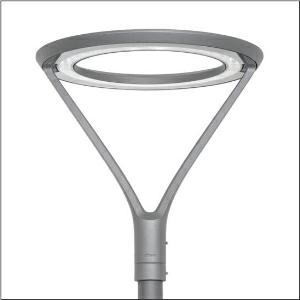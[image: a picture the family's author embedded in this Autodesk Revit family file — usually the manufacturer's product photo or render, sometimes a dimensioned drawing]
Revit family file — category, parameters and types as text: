
# Revit family: dl_r__20___pl1_2s_5xa512832s008_323f
name_source: partatom
category: Lighting Fixtures
units: mm (PartAtom-declared; Revit-internal decimal feet)

## family parameters
Cut with Voids When Loaded = No
Host = Face
Light Source = No
Part Type = Normal
Room Calculation Point = No
Round Connector Dimension = Use Diameter
Shared = No

## types (1)
- --- (1 x LED, 3050 lm, 30.4 W, 2200K)
    Apparent Load = 30 VA
    CIE Flux Codes = 33 78 99 100 100
    Color Rendering = 70
    Color Temperature = 2200K
    Default Elevation = 1800 mm
    Description = DL® 20, mast luminaire, primary light control with reflector, highly specular, primary optical cover: cover, of toughened safety glass of clear glass with excellent transmission level, light distribution: PL1.2s, light emission: direct distribution, primary light characteristic: symmetric, installation type: post-top, LED, High Power LED, rated luminous flux: 3.040lm, luminous efficacy: 86lm/W, light colour: 722, colour temperature: 2200K, control gear: ECG Plus, control: flexible luminous flux parameterisation, time-dependent luminous flux control, constant luminous flux control, digital communication interface, power reduction, overheat protection, electronic power reduction, mains connection: 230..240V, 50/60Hz, connection cable pre-assembled, cable length: 5m, start of lifetime: 36W, end of service life: 36W, reduction: 17W, luminaire housing, upper part, of cast aluminium, powder-coated, Siteco® metallic grey (DB 702S), diameter: 690mm, height: 690mm, spigot size: 76mm (post-top), luminaire housing, of cast aluminium, powder-coated, Siteco® metallic grey (DB 702S), equipment: standard, protection rating (complete): IP66, insulation class (complete): insulation class II (safety insulation), certification: CE, ENEC, VDE, impact resistance: IK08, permissible operating ambient temperature: -25..+35°C, standard-compliant lighting for roads and squares, packaging unit: 1 piece

Light Distribution: PL1.2s
    Height = 690 mm
    Lamp = 1 x LED
    Lamp Light Flux = 3050 lm
    Lamp Power = 30.4 W
    Lamp count = 1
    Length = 690 mm
    Luminous efficacy = 100 lm/W
    Manufacturer = Siteco
    ModVariant = No
    Model = 5XA512832S008
    Number of Poles = 1
    OnlyDefault = Yes
    Power Factor = 1
    Product Name = DL® 20 | PL1.2s
    Product group = mast luminaire | pylon top
    ProductGroupID = 6100
    Protection Class = Protection class II
    Protection Degree = IP 66
    RLX_Detail_Level = 1
    RLX_Emergency_Light_Flux = 0 lm
    RLX_Emergency_Type = 0
    RLX_Emergency_Type_DB = No
    RlxData = <blob elided: 204753 chars, md5=60c489e2>
    Socket = socket
    Standby Power = 0 W
    System Light Flux = 3050 lm
    System Power = 30 W
    Type Comments = factory setting: luminous flux: 100 % | dim-lin: 254 | 412 mA
    Type Image = l_1006001.jpg
    URL = http://relux.com
    VarID = @adj_028093
    Voltage = 0 V
    Weight = 0.00 kg
    Width = 0 mm  [stored 0 ft]

note: [stored X ft] marks values corroborated as IEEE doubles in the binary element streams (Revit-internal decimal feet)

## geometry (parser evidence)
native form markers: Blend x4, Sweep x10
no freeform markers — native parametric forms only
